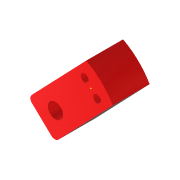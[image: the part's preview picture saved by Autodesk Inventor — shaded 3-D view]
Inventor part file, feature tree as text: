
AUTODESK INVENTOR PART (.ipt)
format: ipt  version: 2022 (Build 260153000, 153)  size: 146,432 bytes
history: native  units: mm
features: reference x5, other x5, sketch x4, extrude x2, fillet x1
ambient origin geometry x8: Origin, YZ Plane, XZ Plane, XY Plane, X Axis, Y Axis, Z Axis, Center Point
bodies: Volumenkörper1 (feature_tree)
feature tree (17):
  extrude  "Extrusion1"  Depth=6.2mm
  sketch  "Skizze2"  dims[d3=3.2mm d4=15.0mm d5=0.0mm]
  sketch  "Skizze3"  dims[d9=2.0mm]
  fillet  "Rundung1"  Radius=3.2mm
  extrude  "Extrusion2"  Depth=15.0mm TaperAngle=0.0deg
  sketch  "Skizze1"  dims[d0=24.0mm d1=6.2mm d2=3.2mm]
  reference  "Referenz1"
  reference  "Referenz2"
  reference  "Referenz3"
  reference  "Referenz4"
  reference  "Referenz5"
  sketch  "Skizze4"  dims[d10=12.0mm d11=5.0mm d12=-0.349066mm]
  other  "Assembly_Matchboxscope_injectionmolded_holo.iam"
  other  "IM_Matchboxscope_Laserholder:1"
  other  "00_laserpointer_red:2"
  other  "00_mk8_nozzle_0.4STEP:1"
  other  "IM_Lensholder:1"
